# Revit family: Power-ModularDevices-GEWISS-90AM-TRANSFORMER_SAFETY
name_source: partatom
category: Apparecchi elettrici
revit_build: Autodesk Revit 2016 (Build: 20161004_0715(x64)
units: mm (PartAtom-declared; Revit-internal decimal feet)

## family parameters
Condiviso = No
Host = Superficie
Mantenere orientamento annotazione = Sì
Numero OmniClass = 23.80.50.00
Punto di calcolo locali = Sì
Quota connettore circolare = Usa diametro
Taglio con vuoti quando caricato = No
Tipo di parte = Normale
Titolo OmniClass = Terminals for Power Supply

## types (4) — shared parameters
Catalogue = POWER
Catalogue Range = 90 AM
Electrocod = 140
IDF = b238ad9a-9cd4-475b-af46-9ddbc1adffda
IDT = 319503f1-0c15-47ce-b8a4-ddc3006a59e7
Immagine tipo = GW96324.jpg
Numero di poli = 1
Operation = Continuous
Primary voltage = 230V
Produttore = GEWISS S.p.A.
Prospetto di default = 1219 mm
SEO = Transformer
Secondary voltage = 12+12=24 V
Spostamento_x = -3300 mm  [stored -10.8268 ft]
TIPO = GENERICO - 90AM TRASFORMATORI DI SICUREZZA : GW96324 Trasformatore di sicurezza 63VA 230V/12+12=24V - 6M
Technical sheet = https://www.gewiss.com
URL = https://www.gewiss.com
Version file RFA = 18.0
carico = Altro
potenza in watt = 0 V
zero-valued in all types: Barra_DIN

## per-type parameters (varying)
| type | Descrizione | EAN code | Modello | No. Chorus modules | No. of modules EN 50022 | Power | Rated power: |
| GW96322 - SAFETY TRANSFORMER 25 VA 230V | SAFETY TRANSFORMER 25 VA 230V | 8011564177062 | GW96322 | 3 | 3 | 25VA (12/24V) | 25 VA (12/24 V) |
| GW96323 - SAFETY TRANSFORMER 40 VA 230V | SAFETY TRANSFORMER 40 VA 230V | 8011564176980 | GW96323 | 4 | 4 | 40VA (12/24V) | 40 VA (12/24 V) |
| GW96324 - SAFETY TRANSFORMER 63 VA 230V | SAFETY TRANSFORMER 63 VA 230V | 8011564177079 | GW96324 | 6 | 6 | 63VA (12/24V) | 63 VA (12/24 V) |
| GW96321 - SAFETY TRANSFORMER 15 VA 230V | SAFETY TRANSFORMER 15 VA 230V | 8011564178717 | GW96321 | 3 | 3 | 15VA (12/24V) | 15 VA (12/24 V) |

note: [stored X ft] marks values corroborated as IEEE doubles in the binary element streams (Revit-internal decimal feet)
